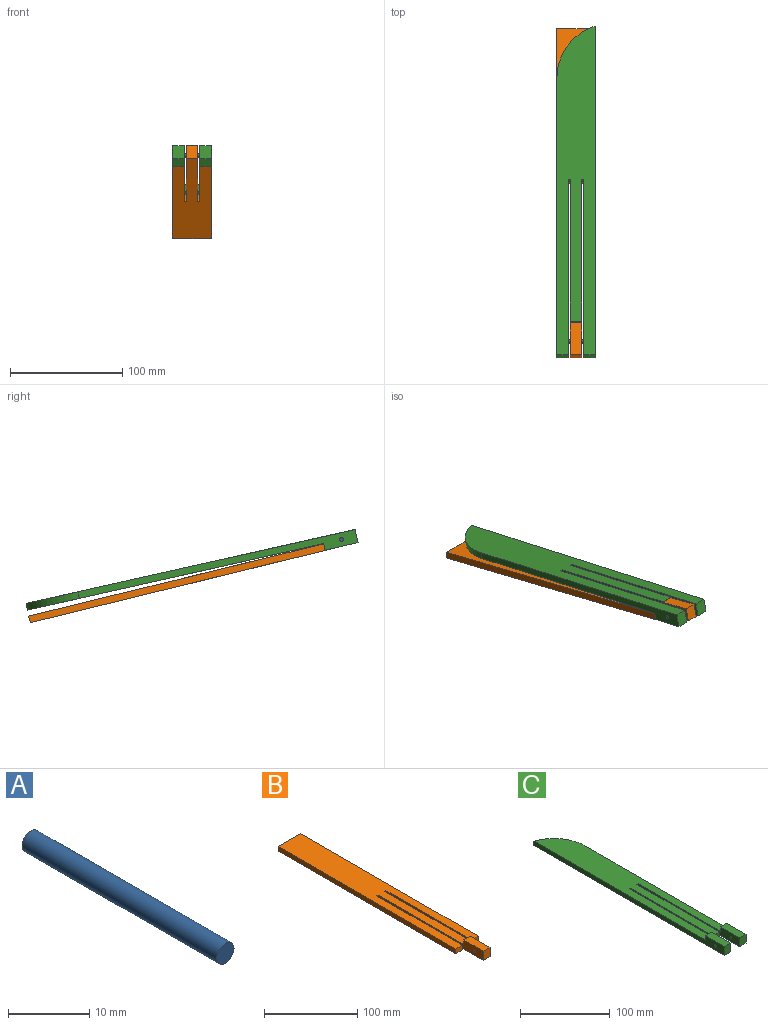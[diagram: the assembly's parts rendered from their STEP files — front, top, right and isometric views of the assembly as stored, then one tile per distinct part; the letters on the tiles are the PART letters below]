
ASSEMBLY  parts=3 mates=3
PART A: 3 faces, bbox 3x34x3 mm
  f0: cylinder r=1.5mm len=34mm, axis (0,1,0), area 320.4mm2, adj f1,f2
  f1: plane 3x3mm, normal (0,-1,0), area 7.1mm2, adj f0
  f2: plane 3x3mm, normal (0,1,0), area 7.1mm2, adj f0
PART B: 17 faces, bbox 34x300x12 mm
  f0: plane 270x34mm, normal (0,0,1), area 8660mm2, adj f1,f3,f4,f5,f6,f7,f8,f9
  f1: plane 160x12mm, normal (-1,0,0), area 1132.9mm2, adj f0,f2,f12,f13,f14,f15,f16
  f2: plane 12x10mm, normal (0,-1,0), area 120mm2, adj f1,f3,f13,f15
  f3: plane 160x12mm, normal (1,0,0), area 1132.9mm2, adj f0,f2,f4,f13,f14,f15,f16
  f4: plane 6x2mm, normal (0,-1,0), area 12mm2, adj f0,f3,f5,f13
  f5: plane 130x6mm, normal (-1,0,0), area 780mm2, adj f0,f4,f6,f13
  f6: plane 10x6mm, normal (0,-1,0), area 60mm2, adj f0,f5,f7,f13
  f7: plane 270x6mm, normal (1,0,0), area 1620mm2, adj f0,f6,f8,f13
  f8: plane 34x6mm, normal (0,1,0), area 204mm2, adj f0,f7,f9,f13
  f9: plane 270x6mm, normal (-1,0,0), area 1620mm2, adj f0,f8,f10,f13
  f10: plane 10x6mm, normal (0,-1,0), area 60mm2, adj f0,f9,f11,f13
  f11: plane 130x6mm, normal (1,0,0), area 780mm2, adj f0,f10,f12,f13
  f12: plane 6x2mm, normal (0,-1,0), area 12mm2, adj f0,f1,f11,f13
  f13: plane 300x34mm, normal (0,0,-1), area 8960mm2, adj f1,f2,f3,f4,f5,f6,f7,f8
  f14: plane 10x6mm, normal (0,1,0), area 60mm2, adj f0,f1,f3,f15
  f15: plane 30x10mm, normal (0,0,1), area 300mm2, adj f1,f2,f3,f14
  f16: cylinder r=1.5mm len=10mm, axis (-1,0,0), area 94.2mm2, adj f1,f3
PART C: 20 faces, bbox 34x300x12 mm
  f0: plane 270x34mm, normal (0,0,1), area 8226.8mm2, adj f1,f2,f3,f4,f5,f6,f7,f9
  f1: plane 160x12mm, normal (1,0,0), area 1132.9mm2, adj f0,f2,f11,f12,f13,f14,f18
  f2: plane 6x2mm, normal (0,-1,0), area 12mm2, adj f0,f1,f3,f12
  f3: plane 130x6mm, normal (-1,0,0), area 780mm2, adj f0,f2,f4,f12
  f4: plane 10x6mm, normal (0,-1,0), area 60mm2, adj f0,f3,f5,f12
  f5: plane 130x6mm, normal (1,0,0), area 780mm2, adj f0,f4,f6,f12
  f6: plane 6x2mm, normal (0,-1,0), area 12mm2, adj f0,f5,f7,f12
  f7: plane 160x12mm, normal (-1,0,0), area 1132.9mm2, adj f0,f6,f8,f12,f15,f16,f17
  f8: plane 12x10mm, normal (0,-1,0), area 120mm2, adj f7,f9,f12,f16
  f9: plane 252.63x12mm, normal (1,0,0), area 1688.7mm2, adj f0,f8,f12,f15,f16,f17,f19
  f10: plane 300x12mm, normal (-1,0,0), area 1972.9mm2, adj f0,f11,f12,f13,f14,f18,f19
  f11: plane 12x10mm, normal (0,-1,0), area 120mm2, adj f1,f10,f12,f14
  f12: plane 300x34mm, normal (0,0,-1), area 8826.8mm2, adj f1,f2,f3,f4,f5,f6,f7,f8
  f13: plane 10x6mm, normal (0,1,0), area 60mm2, adj f0,f1,f10,f14
  f14: plane 30x10mm, normal (0,0,1), area 300mm2, adj f1,f10,f11,f13
  f15: plane 10x6mm, normal (0,1,0), area 60mm2, adj f0,f7,f9,f16
  f16: plane 30x10mm, normal (0,0,1), area 300mm2, adj f7,f8,f9,f15
  f17: cylinder r=1.5mm len=10mm, axis (-1,0,0), area 94.2mm2, adj f7,f9
  f18: cylinder r=1.5mm len=10mm, axis (-1,0,0), area 94.2mm2, adj f1,f10
  f19: cylinder r=50mm len=47.37mm, axis (0,0,-1), area 373.5mm2, adj f0,f9,f10,f12
PLACE A rot(axis=(0.71,0.71,0),180deg) t=(-91.34,-142.05,158.06)mm fixed
PLACE B rot(axis=(-1,0,0),13.8deg) t=(-89.25,-86.17,138.41)mm
PLACE C rot(axis=(0,0.99,-0.11),180deg) t=(-91.34,-7.75,134.24)mm
MATE revolute C.f17 <-> A.f0  axis (1,0,0) through (-74.34,-142.05,158.28)mm
MATE cylindrical A.f0 <-> C.f17  axis (1,0,0) through (-74.34,-142.05,158.28)mm
MATE revolute B.f16 <-> A.f0  axis (-1,0,0) through (-86.34,-142.05,158.28)mm
